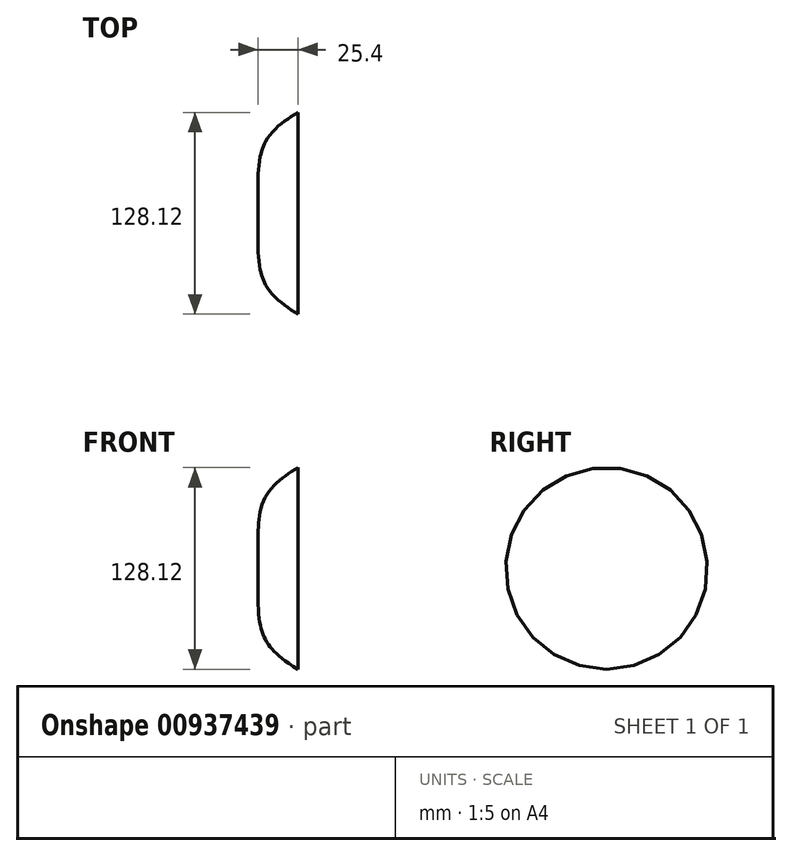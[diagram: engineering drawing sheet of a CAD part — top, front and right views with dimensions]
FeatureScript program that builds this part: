
annotation { "Feature Type Name" : "Feature", "Feature Type Description" : "" }
export const myFeature = defineFeature(function(context is Context, id is Id, definition is map)
    precondition{}
    {
        {
            var Q0;
            Q0=qCreatedBy(makeId("Right.planeOp"),FACE);
            var sketch = newSketch(context, id + "F0", { "sketchPlane" : qUnion([Q0])});
            skCircle(sketch, "E0", {"center": v(0, 0) * mm, "radius": 64.06 * mm});
            skSolve(sketch);
        }
        {
            var Q0;
            Q0=makeQuery(id+"F0.imprint","IMPRINT",FACE,{"disambiguationData":[TD([[makeQuery(id+"F0.imprint","IMPRINT",EDGE,{"derivedFrom":sQuery(id+"F0.wireOp",EDGE,"E0")}),1.0]])]});
            var Q1;
            Q1=sQuery(id+"F0.wireOp",EDGE,"E0");
            extrude(context, id + "F1", {"entities" : qUnion([Q0]), "surfaceEntities" : qUnion([Q1]), "depth" : 25.4 * mm, "offsetDistance" : 25.4 * mm});
        }
        {
            var Q0;
            Q0=makeQuery(id+"F1.opExtrude","CAP_EDGE",EDGE,{"disambiguationData":[OSD([sQuery(id+"F0.wireOp",EDGE,"E0")])],"isStart":true});
            fillet(context, id + "F2", {"entities" : qUnion([Q0]), "radius" : 52.12 * mm, "tangentPropagation" : true, "rho" : 0.6, "crossSection" : FilletCrossSection.CONIC, "allowEdgeOverflow" : false});
        }
    });
